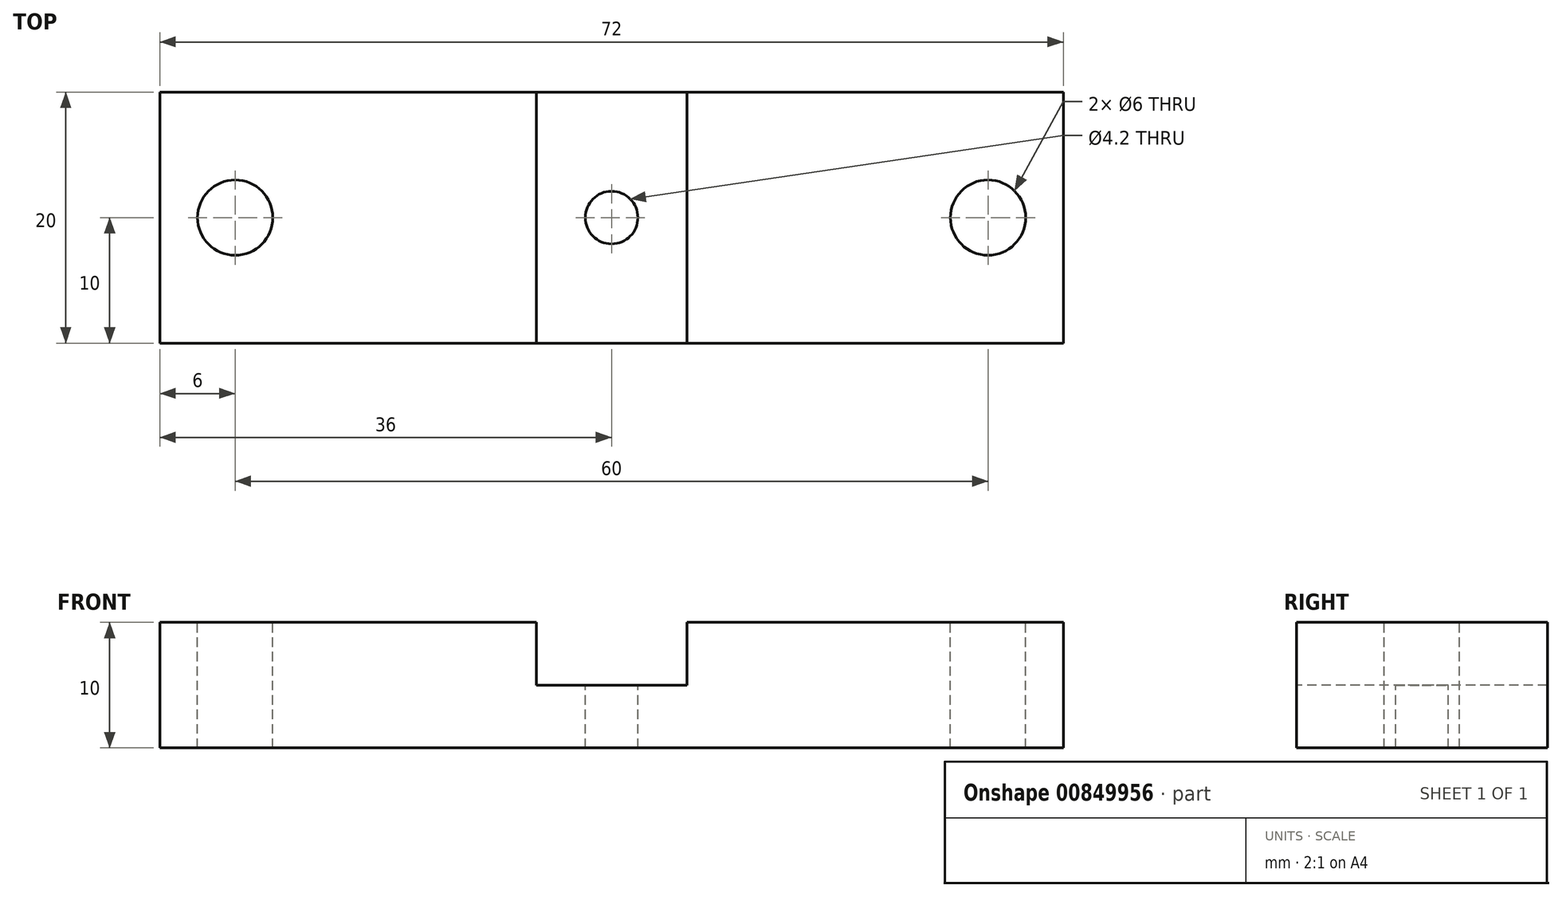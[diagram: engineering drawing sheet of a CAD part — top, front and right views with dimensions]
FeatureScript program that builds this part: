
annotation { "Feature Type Name" : "Feature", "Feature Type Description" : "" }
export const myFeature = defineFeature(function(context is Context, id is Id, definition is map)
    precondition{}
    {
        {
            var Q0;
            Q0=qCreatedBy(makeId("Top.planeOp"),FACE);
            var sketch = newSketch(context, id + "F0", { "sketchPlane" : qUnion([Q0])});
            skLineSegment(sketch, "E0.bottom", {"start": v(0, 0) * mm, "end": v(72, 0) * mm});
            skLineSegment(sketch, "E0.top", {"start": v(0, 20) * mm, "end": v(72, 20) * mm});
            skLineSegment(sketch, "E0.left", {"start": v(0, 0) * mm, "end": v(0, 20) * mm});
            skLineSegment(sketch, "E0.right", {"start": v(72, 0) * mm, "end": v(72, 20) * mm});
            skSolve(sketch);
        }
        {
            var Q0;
            Q0 = qSketchRegion(id + "F0", true);
            extrude(context, id + "F1", {"entities" : qUnion([Q0]), "depth" : 10 * mm, "offsetDistance" : 25.4 * mm});
        }
        {
            var Q0;
            Q0=makeQuery(id+"F1.opExtrude","CAP_FACE",FACE,{"disambiguationData":[OSD([sQuery(id+"F0.wireOp",EDGE,"E0.bottom"),sQuery(id+"F0.wireOp",EDGE,"E0.top"),sQuery(id+"F0.wireOp",EDGE,"E0.left"),sQuery(id+"F0.wireOp",EDGE,"E0.right")])],"isStart":false});
            var sketch = newSketch(context, id + "F2", { "sketchPlane" : qUnion([Q0])});
            skLineSegment(sketch, "E1.bottom", {"start": v(30, 20) * mm, "end": v(42, 20) * mm});
            skLineSegment(sketch, "E1.top", {"start": v(30, 0) * mm, "end": v(42, 0) * mm});
            skLineSegment(sketch, "E1.left", {"start": v(30, 20) * mm, "end": v(30, 0) * mm});
            skLineSegment(sketch, "E1.right", {"start": v(42, 20) * mm, "end": v(42, 0) * mm});
            skSolve(sketch);
        }
        {
            var Q0;
            Q0 = qSketchRegion(id + "F2", true);
            extrude(context, id + "F3", {"entities" : qUnion([Q0]), "operationType" : NewBodyOperationType.REMOVE, "oppositeDirection" : true, "depth" : 5 * mm, "offsetDistance" : 25 * mm});
        }
        {
            var Q0;
            {var subQ0=sQuery(id+"F0.wireOp",EDGE,"E0.bottom");var subQ1=sQuery(id+"F0.wireOp",EDGE,"E0.top");var subQ2=sQuery(id+"F0.wireOp",EDGE,"E0.left");Q0=makeQuery(id+"F3.boolean.opBoolean","SPLIT",FACE,{"disambiguationData":[TD([makeQuery(id+"F1.opExtrude","SWEPT_FACE",FACE,{"disambiguationData":[OSD([subQ2])]})])],"derivedFrom":makeQuery(id+"F1.opExtrude","CAP_FACE",FACE,{"disambiguationData":[OSD([subQ0,subQ1,subQ2,sQuery(id+"F0.wireOp",EDGE,"E0.right")])],"isStart":false})});}
            var sketch = newSketch(context, id + "F4", { "sketchPlane" : qUnion([Q0])});
            skCircle(sketch, "E2", {"center": v(6, 10) * mm, "radius": 3 * mm});
            skCircle(sketch, "E3", {"center": v(66, 10) * mm, "radius": 3 * mm});
            skCircle(sketch, "E4", {"center": v(36, 10) * mm, "radius": 2.1 * mm});
            skSolve(sketch);
        }
        {
            var Q0;
            Q0 = qSketchRegion(id + "F4", true);
            extrude(context, id + "F5", {"entities" : qUnion([Q0]), "operationType" : NewBodyOperationType.REMOVE, "oppositeDirection" : true, "depth" : 25 * mm, "offsetDistance" : 25 * mm});
        }
    });
